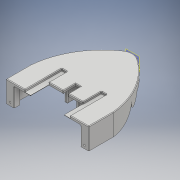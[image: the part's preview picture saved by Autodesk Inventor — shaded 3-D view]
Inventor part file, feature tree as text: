
AUTODESK INVENTOR PART (.ipt)
format: ipt  version: 2018 (Build 220112000, 112)  size: 1,123,328 bytes
history: native  units: mm
features: projected_geometry x66, reference x34, extrude x25, sketch x24, fillet x18, other x15, plane x5
ambient origin geometry x8: Origin, YZ Plane, XZ Plane, XY Plane, X Axis, Y Axis, Z Axis, Center Point
bodies: Solid1 (feature_tree)
feature tree (187):
  extrude  "Extrusion1"  Depth=40.0mm
  sketch  "Sketch3"  dims[d4=110.0mm d5=130.0mm]
  plane  "Work Plane1"
  extrude  "Extrusion2"  Depth=130.0mm
  extrude  "Extrusion3"  Depth=20.0mm
  extrude  "Extrusion4"  Depth=10.0mm TaperAngle=0.0deg
  extrude  "Extrusion5"  Depth=20.0mm
  extrude  "Extrusion6"  Depth=10.0mm
  extrude  "Extrusion7"  Depth=50.0mm
  extrude  "Extrusion8"  Depth=25.0mm TaperAngle=0.0deg
  extrude  "Extrusion9"  Depth=5.0mm TaperAngle=0.0deg
  fillet  "Fillet1"  Radius=160.0mm
  extrude  "Extrusion10"  Depth=20.0mm TaperAngle=0.0deg
  extrude  "Extrusion11"  Depth=160.0mm TaperAngle=0.0deg
  extrude  "Extrusion12"  Depth=6.0mm
  sketch  "Sketch16"  dims[d72=160.0mm d73=0.0mm d74=6.0mm]
  plane  "Work Plane2"
  extrude  "Extrusion13"  Depth=1.0mm
  fillet  "Fillet2"  Radius=60.0mm
  fillet  "Fillet3"  Radius=1.0mm
  fillet  "Fillet4"  Radius=8.35mm
  fillet  "Fillet5"  Radius=10.0mm
  extrude  "Extrusion14"  Depth=4.118mm
  fillet  "Fillet6"  Radius=4.572mm
  plane  "Work Plane3"
  extrude  "Extrusion15"  Depth=16.002mm
  extrude  "Extrusion16"  Depth=10.0mm TaperAngle=0.0deg
  sketch  "Sketch20"  dims[d87=2.94mm d88=16.002mm]
  plane  "Work Plane4"
  extrude  "Extrusion17"  Depth=1.0mm
  sketch  "Sketch21"  dims[d89=8.0mm d90=10.0mm d91=0.0mm]
  plane  "Work Plane5"
  extrude  "Extrusion18"  Depth=1.0mm
  fillet  "Fillet8"  Radius=1.0mm
  fillet  "Fillet9"  Radius=1.0mm
  fillet  "Fillet10"  Radius=10.0mm
  fillet  "Fillet11"  Radius=1.0mm
  fillet  "Fillet12"  Radius=10.0mm
  fillet  "Fillet13"  Radius=5.0mm
  extrude  "Extrusion19"  Depth=5.0mm
  extrude  "Extrusion20"  Depth=20.0mm
  fillet  "Fillet14"  Radius=10.0mm
  fillet  "Fillet15"  Radius=20.0mm
  extrude  "Extrusion21"  Depth=2.0mm
  fillet  "Fillet16"  Radius=2.0mm
  extrude  "Extrusion22"  Depth=0.2mm
  extrude  "Extrusion23"  Depth=2.0mm
  fillet  "Fillet17"  Radius=2.0mm
  extrude  "Extrusion24"  Depth=1.0mm
  extrude  "Extrusion25"  Depth=2.0mm
  fillet  "Fillet18"  Radius=4.0mm
  fillet  "Fillet19"  Radius=10.0mm
  sketch  "Sketch1"  dims[d2=40.0mm d3=40.0mm]
  reference  "Reference1"
  reference  "Reference2"
  other  "Work Point1"
  sketch  "Sketch5"  dims[d6=130.0mm d7=20.0mm]
  sketch  "Sketch6"  dims[d8=20.0mm d9=10.0mm d10=0.0mm]
  sketch  "Sketch8"  dims[d17=40.0mm d18=20.0mm]
  sketch  "Sketch9"  dims[d19=40.0mm d20=10.0mm]
  projected_geometry  "Projected Loop1"
  projected_geometry  "Projected Loop2"
  projected_geometry  "Projected Loop3"
  projected_geometry  "Projected Loop4"
  sketch  "Sketch10"  dims[d21=50.0mm d22=50.0mm]
  sketch  "Sketch11"  dims[d23=35.0mm d24=0.0mm d25=25.0mm d26=0.0mm]
  sketch  "Sketch12"  dims[d27=160.0mm d28=0.0mm]
  reference  "Reference3"
  reference  "Reference4"
  reference  "Reference5"
  reference  "Reference6"
  reference  "Reference7"
  projected_geometry  "Projected Loop5"
  projected_geometry  "Projected Loop6"
  sketch  "Sketch13"  dims[d53=36.0mm d54=36.0mm d55=99.0mm d56=117.0mm d57=117.0mm d58=18.0mm d59=18.0mm d60=160.0mm d61=5.0mm d62=0.0mm d63=0.0mm d64=160.0mm d65=0.0mm]
  projected_geometry  "Projected Loop7"
  sketch  "Sketch14"  dims[d66=20.0mm d67=12.5mm d68=0.0mm]
  reference  "Reference8"
  sketch  "Sketch15"  dims[d69=25.0mm d70=160.0mm d71=0.0mm]
  reference  "Reference9"
  reference  "Reference10"
  reference  "Reference11"
  reference  "Reference12"
  reference  "Reference13"
  reference  "Reference14"
  reference  "Reference15"
  projected_geometry  "Projected Loop8"
  reference  "Reference16"
  reference  "Reference17"
  reference  "Reference18"
  reference  "Reference19"
  reference  "Reference20"
  reference  "Reference21"
  reference  "Reference22"
  reference  "Reference23"
  reference  "Reference24"
  reference  "Reference25"
  reference  "Reference26"
  reference  "Reference27"
  sketch  "Sketch17"  dims[d75=40.0mm d76=0.0mm d77=1.0mm d78=60.0mm d79=0.0mm d80=1.0mm d81=8.35mm d82=10.0mm d83=0.0mm]
  reference  "Reference28"
  reference  "Reference29"
  reference  "Reference30"
  projected_geometry  "Projected Loop9"
  projected_geometry  "Projected Loop10"
  projected_geometry  "Projected Loop11"
  projected_geometry  "Projected Loop12"
  projected_geometry  "Projected Loop13"
  projected_geometry  "Projected Loop14"
  projected_geometry  "Projected Loop15"
  projected_geometry  "Projected Loop16"
  projected_geometry  "Projected Loop17"
  projected_geometry  "Projected Loop18"
  projected_geometry  "Projected Loop19"
  projected_geometry  "Projected Loop20"
  projected_geometry  "Projected Loop21"
  projected_geometry  "Projected Loop22"
  projected_geometry  "Projected Loop23"
  projected_geometry  "Projected Loop24"
  projected_geometry  "Projected Loop25"
  projected_geometry  "Projected Loop26"
  projected_geometry  "Projected Loop27"
  projected_geometry  "Projected Loop28"
  projected_geometry  "Projected Loop29"
  projected_geometry  "Projected Loop30"
  projected_geometry  "Projected Loop31"
  projected_geometry  "Projected Loop32"
  projected_geometry  "Projected Loop33"
  projected_geometry  "Projected Loop34"
  projected_geometry  "Projected Loop35"
  projected_geometry  "Projected Loop36"
  projected_geometry  "Projected Loop37"
  projected_geometry  "Projected Loop38"
  projected_geometry  "Projected Loop39"
  projected_geometry  "Projected Loop40"
  projected_geometry  "Projected Loop41"
  projected_geometry  "Projected Loop42"
  projected_geometry  "Projected Loop43"
  projected_geometry  "Projected Loop44"
  projected_geometry  "Projected Loop45"
  projected_geometry  "Projected Loop46"
  projected_geometry  "Projected Loop47"
  projected_geometry  "Projected Loop48"
  projected_geometry  "Projected Loop49"
  projected_geometry  "Projected Loop50"
  projected_geometry  "Projected Loop51"
  projected_geometry  "Projected Loop52"
  projected_geometry  "Projected Loop53"
  projected_geometry  "Projected Loop54"
  projected_geometry  "Projected Loop55"
  projected_geometry  "Projected Loop56"
  projected_geometry  "Projected Loop57"
  projected_geometry  "Projected Loop58"
  projected_geometry  "Projected Loop59"
  projected_geometry  "Projected Loop60"
  projected_geometry  "Projected Loop61"
  projected_geometry  "Projected Loop62"
  sketch  "Sketch19"  dims[d84=0.2mm d85=4.118mm d86=4.572mm]
  reference  "Reference31"
  projected_geometry  "Projected Loop63"
  projected_geometry  "Projected Loop64"
  projected_geometry  "Projected Loop65"
  projected_geometry  "Projected Loop66"
  sketch  "Sketch22"  dims[d92=1.0mm d93=1.0mm]
  reference  "Reference33"
  sketch  "Sketch23"  dims[d94=1.0mm d95=1.0mm d96=1.0mm d97=1.0mm d98=10.0mm d99=0.0mm d100=1.0mm d101=10.0mm d102=0.0mm d103=5.0mm]
  sketch  "Sketch24"  dims[d104=5.0mm d105=2.5mm]
  reference  "Reference34"
  sketch  "Sketch25"  dims[d106=18.0mm d107=2.5mm d108=10.0mm d109=0.0mm d110=20.0mm]
  reference  "Reference35"
  sketch  "Sketch26"  dims[d111=9.75mm d112=19.5mm d113=2.0mm]
  sketch  "Sketch27"  dims[d114=0.2mm d115=0.2mm]
  sketch  "Sketch28"  dims[d116=2.4mm d117=2.0mm d118=2.0mm d119=4.0mm d120=2.0mm d121=4.0mm d122=10.0mm d123=0.0mm d124=25.5mm d125=10.0mm d126=0.0mm d128=1.0mm d129=1.0mm d130=1.0mm d131=1.0mm d132=1.0mm d133=0.5mm d134=10.0mm d135=10.0mm d136=2.0mm d137=2.0mm d138=5.0mm d139=20.0mm d140=5.0mm d141=20.0mm d142=4.85mm d143=9.7mm d144=3.0mm d145=20.0mm d146=0.0mm d147=3.0mm d148=2.5mm d149=20.0mm d150=0.0mm d151=1.0mm d152=1.0mm d153=10.0mm d154=0.0mm d155=1.0mm d156=2.75mm d157=10.0mm d158=0.0mm d159=70.0mm d160=25.0mm d161=10.0mm d162=0.0mm d163=1.0mm d164=30.0mm d165=4.0mm d166=8.0mm d167=20.0mm d168=100.0mm d169=0.0mm d170=100.0mm d171=0.0mm d172=1.0mm d173=1.0mm]
  other  "<userpath>\OneDrive\Documents\Inventor\TSA\2018\Animatronics\Tortoise\Head\HeadAssembly.iam"
  other  "HeadAssembly.iam"
  other  "HeadBase:1"
  other  "Rack:2"
  other  "Rack:1"
  other  "HeadTop:1"
  other  "<userpath>\OneDrive\Documents\Inventor\TSA\2018\Animatronics\Tortoise\TurtleAssembly.iam"
  other  "TurtleAssembly.iam"
  other  "servo (2):4"
  other  "servo (2):5"
  other  "SyringeConnector:1"
  other  "Syringe:2"
  other  "SyringEnd:1"
  other  "FlexHinge:1"
